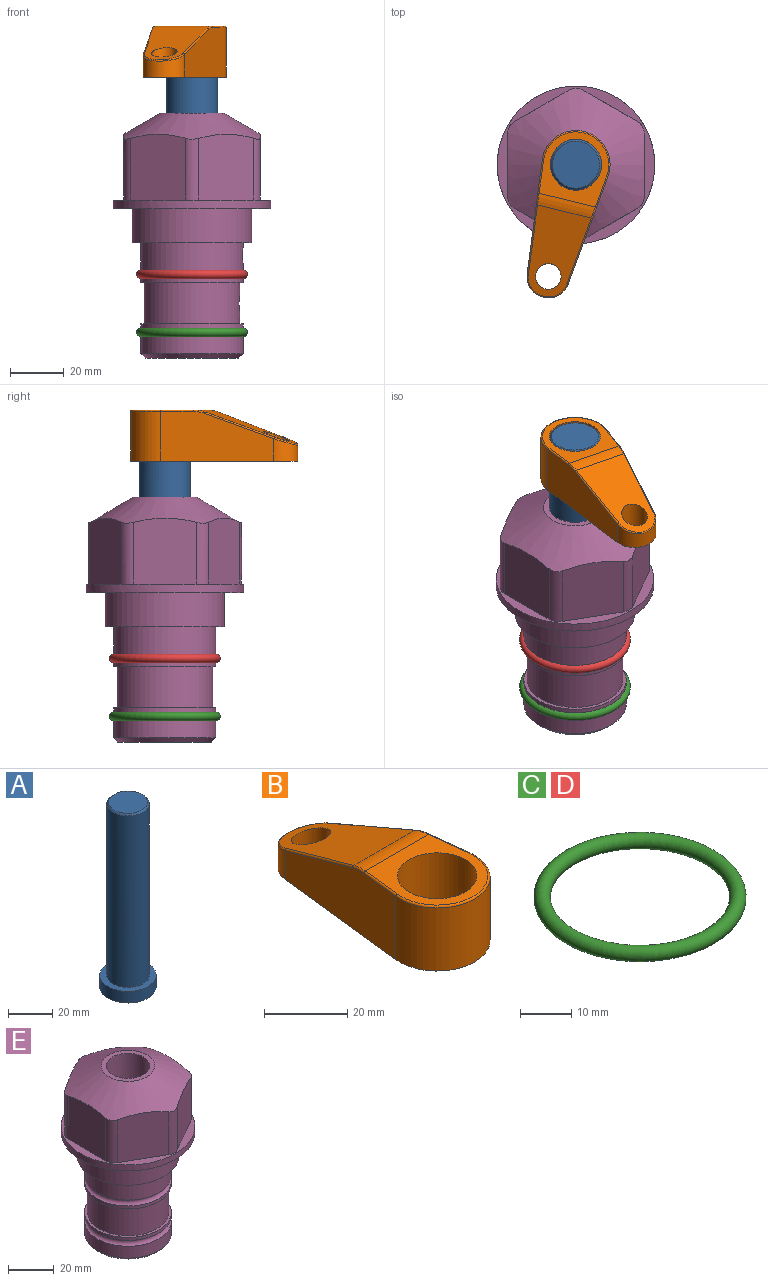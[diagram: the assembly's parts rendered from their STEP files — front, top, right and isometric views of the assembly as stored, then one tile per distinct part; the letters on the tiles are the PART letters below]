
ASSEMBLY  parts=5 mates=3
PART A: 6 faces, bbox 25.4x25.4x101.6 mm
  f0: plane 17.46x17.46mm, normal (0,0,1), area 239.5mm2, adj f5
  f1: plane 25.4x25.4mm, normal (0,0,-1), area 506.7mm2, adj f2
  f2: cylinder r=12.7mm len=25.4mm, axis (0,0,1), area 506.7mm2, adj f1,f3
  f3: plane 25.4x25.4mm, normal (0,0,1), area 221.7mm2, adj f2,f4
  f4: cylinder r=9.53mm len=94.46mm, axis (0,0,1), area 5653mm2, adj f3,f5
  f5: cone r=8.73mm half-angle=45deg, axis (0,0,-1), area 64.4mm2, adj f0,f4
PART B: 44 faces, bbox 27.5x64.5x19.1 mm
  f0: plane 2.3x0.95mm, normal (0,0,-1), area 1mm2, adj f25,f30,f34
  f1: plane 63.5x25.4mm, normal (0,0,-1), area 561.7mm2, adj f2,f3,f4,f5,f6,f7,f19,f20
  f2: cylinder r=12.7mm len=25.4mm, axis (0,0,-1), area 792.2mm2, adj f1,f3,f5,f13
  f3: plane 42.33x18.54mm, normal (0.99,0.11,0), area 647mm2, adj f1,f2,f4,f11,f12,f14
  f4: cylinder r=7.94mm len=15.78mm, axis (0,0,-1), area 158.6mm2, adj f1,f3,f5,f16
  f5: plane 42.33x18.54mm, normal (-0.99,0.11,0), area 647mm2, adj f1,f2,f4,f15,f17,f18
  f6: cylinder r=9.53mm len=19.05mm, axis (0,0,-1), area 1140.1mm2, adj f1,f8
  f7: cylinder r=4.76mm len=10.98mm, axis (0,0,-1), area 276.1mm2, adj f1,f9
  f8: plane 25.83x24.38mm, normal (0,0,1), area 262.2mm2, adj f6,f10,f11,f13,f15
  f9: plane 32.49x20.55mm, normal (0,0.34,0.94), area 489.9mm2, adj f7,f10,f14,f16,f18
  f10: cylinder r=12.7mm len=21.49mm, axis (-1,0,0), area 93.2mm2, adj f8,f9,f12,f17
  f11: cylinder r=0.51mm len=12.34mm, axis (0.11,-0.99,0), area 9.9mm2, adj f3,f8,f12,f13
  f12: bspline ~7.62x1.64mm, area 3.5mm2, adj f3,f10,f11,f14
  f13: torus R=12.19mm, axis (0,0,1), area 33.6mm2, adj f2,f8,f11,f15
  f14: cylinder r=0.51mm len=26.01mm, axis (0.1,-0.93,0.34), area 21.6mm2, adj f3,f9,f12,f16
  f15: cylinder r=0.51mm len=12.34mm, axis (0.11,0.99,0), area 9.9mm2, adj f5,f8,f13,f17
  f16: bspline ~15.78x7.05mm, area 15.7mm2, adj f4,f9,f14,f18
  f17: bspline ~7.62x1.64mm, area 3.5mm2, adj f5,f10,f15,f18
  f18: cylinder r=0.51mm len=26.01mm, axis (0.1,0.93,-0.34), area 21.6mm2, adj f5,f9,f16,f17
  f19: plane 21.6x14.29mm, normal (-0.99,-0.11,0), area 242.6mm2, adj f1,f26,f28,f34,f36,f38
  f20: plane 21.6x14.29mm, normal (0.99,-0.11,0), area 242.6mm2, adj f1,f27,f29,f37,f39,f41
  f21: cylinder r=12.7mm len=14.29mm, axis (0,0,-1), area 173.2mm2, adj f1,f26,f27,f30,f31,f33
  f22: cylinder r=7.94mm len=7.63mm, axis (0,0,-1), area 53.8mm2, adj f1,f28,f29,f42
  f23: plane 2.3x0.95mm, normal (0,0,-1), area 1mm2, adj f25,f33,f37
  f24: plane 17.94x12.32mm, normal (0,-0.34,-0.94), area 191.2mm2, adj f25,f38,f41,f42
  f25: cylinder r=9.53mm len=12.93mm, axis (-1,0,0), area 37.5mm2, adj f0,f23,f24,f31,f36,f39
  f26: cylinder r=1.59mm len=14.29mm, axis (0,0,-1), area 49mm2, adj f1,f19,f21,f32
  f27: cylinder r=1.59mm len=14.29mm, axis (0,0,-1), area 49mm2, adj f1,f20,f21,f35
  f28: cylinder r=1.59mm len=7.28mm, axis (0,0,-1), area 22.1mm2, adj f1,f19,f22,f40
  f29: cylinder r=1.59mm len=7.28mm, axis (0,0,-1), area 22.1mm2, adj f1,f20,f22,f43
  f30: torus R=14.29mm, axis (0,0,1), area 5.8mm2, adj f0,f21,f31,f32
  f31: bspline ~11.06x2.73mm, area 20.8mm2, adj f21,f25,f30,f33
  f32: sphere r=1.59mm, area 5.4mm2, adj f26,f30,f34
  f33: torus R=14.29mm, axis (0,0,1), area 5.8mm2, adj f21,f23,f31,f35
  f34: cylinder r=1.59mm len=1.68mm, axis (-0.11,0.99,0), area 2.4mm2, adj f0,f19,f32,f36
  f35: sphere r=1.59mm, area 5.4mm2, adj f27,f33,f37
  f36: bspline ~5.82x2.33mm, area 7.7mm2, adj f19,f25,f34,f38
  f37: cylinder r=1.59mm len=1.68mm, axis (0.11,0.99,0), area 2.4mm2, adj f20,f23,f35,f39
  f38: cylinder r=1.59mm len=18.33mm, axis (0.1,-0.93,0.34), area 46.7mm2, adj f19,f24,f36,f40
  f39: bspline ~5.82x2.33mm, area 7.7mm2, adj f20,f25,f37,f41
  f40: sphere r=1.59mm, area 3.6mm2, adj f28,f38,f42
  f41: cylinder r=1.59mm len=18.33mm, axis (0.1,0.93,-0.34), area 46.7mm2, adj f20,f24,f39,f43
  f42: bspline ~8.31x1.84mm, area 15.3mm2, adj f22,f24,f40,f43
  f43: sphere r=1.59mm, area 3.6mm2, adj f29,f41,f42
PART C: 1 faces, bbox 44.7x44.7x3.2 mm
  f0: torus R=19.05mm, axis (0,0,1), area 1193.9mm2
PART D: same geometry as C
PART E: 36 faces, bbox 58.7x58.7x91.2 mm
  f0: cylinder r=17.78mm len=35.56mm, axis (0,0,1), area 1670.8mm2, adj f23,f24,f31
  f1: cylinder r=19.05mm len=38.1mm, axis (0,0,1), area 1191.9mm2, adj f26,f27,f30
  f2: plane 58.66x58.66mm, normal (0,0,-1), area 1150.6mm2, adj f3,f28
  f3: cylinder r=29.33mm len=58.66mm, axis (0,0,-1), area 585.1mm2, adj f2,f4
  f4: plane 58.66x58.66mm, normal (0,0,1), area 475.9mm2, adj f3,f5,f6,f7,f8,f9,f10,f11
  f5: plane 24.5x20.32mm, normal (-0.5,0.87,0), area 562.8mm2, adj f4,f15,f16,f17
  f6: plane 24.5x20.32mm, normal (0.5,0.87,0), area 562.8mm2, adj f4,f14,f15,f17
  f7: plane 24.5x23.48mm, normal (1,0,0), area 562.8mm2, adj f4,f13,f14,f17
  f8: plane 24.5x20.32mm, normal (0.5,-0.87,0), area 562.8mm2, adj f4,f12,f13,f17
  f9: plane 24.5x20.32mm, normal (-0.5,-0.87,0), area 562.8mm2, adj f4,f11,f12,f17
  f10: plane 24.5x23.48mm, normal (-1,0,0), area 562.8mm2, adj f4,f11,f16,f17
  f11: cylinder r=5.08mm len=23.01mm, axis (0,0,-1), area 121.2mm2, adj f4,f9,f10,f17
  f12: cylinder r=5.08mm len=23.01mm, axis (0,0,-1), area 121.2mm2, adj f4,f8,f9,f17
  f13: cylinder r=5.08mm len=23.01mm, axis (0,0,-1), area 121.2mm2, adj f4,f7,f8,f17
  f14: cylinder r=5.08mm len=23.01mm, axis (0,0,-1), area 121.2mm2, adj f4,f6,f7,f17
  f15: cylinder r=5.08mm len=23.01mm, axis (0,0,-1), area 121.2mm2, adj f4,f5,f6,f17
  f16: cylinder r=5.08mm len=23.01mm, axis (0,0,-1), area 121.2mm2, adj f4,f5,f10,f17
  f17: cone r=11.73mm half-angle=60deg, axis (0,0,-1), area 2071.8mm2, adj f5,f6,f7,f8,f9,f10,f11,f12
  f18: plane 23.46x23.46mm, normal (0,0,1), area 147.4mm2, adj f17,f35
  f19: plane 34.93x34.93mm, normal (0,0,-1), area 958mm2, adj f29
  f20: cylinder r=19.05mm len=38.1mm, axis (0,0,1), area 760.1mm2, adj f21,f29
  f21: torus R=19.05mm, axis (0,0,1), area 565.3mm2, adj f20,f22
  f22: cylinder r=19.05mm len=38.1mm, axis (0,0,1), area 190mm2, adj f21,f23
  f23: plane 38.1x38.1mm, normal (0,0,1), area 146.9mm2, adj f0,f22
  f24: plane 38.1x38.1mm, normal (0,0,-1), area 146.9mm2, adj f0,f25
  f25: cylinder r=19.05mm len=38.1mm, axis (0,0,1), area 190mm2, adj f24,f26
  f26: torus R=19.05mm, axis (0,0,1), area 565.3mm2, adj f1,f25
  f27: plane 44.45x44.45mm, normal (0,0,-1), area 411.7mm2, adj f1,f28
  f28: cylinder r=22.23mm len=44.45mm, axis (0,0,1), area 1773.5mm2, adj f2,f27
  f29: cone r=19.05mm half-angle=45deg, axis (0,0,1), area 257.5mm2, adj f19,f20
  f30: cylinder r=3.17mm len=6.75mm, axis (-1,0,0), area 128mm2, adj f1,f33
  f31: cylinder r=3.17mm len=6.35mm, axis (-1,0,0), area 102.5mm2, adj f0,f33
  f32: plane 25.4x25.4mm, normal (0,0,1), area 506.7mm2, adj f33
  f33: cylinder r=12.7mm len=66.42mm, axis (0,0,-1), area 5236.2mm2, adj f30,f31,f32,f34
  f34: cone r=9.53mm half-angle=30deg, axis (0,0,-1), area 443.4mm2, adj f33,f35
  f35: cylinder r=9.53mm len=19.05mm, axis (0,0,-1), area 849mm2, adj f18,f34
PLACE A rot(axis=(0,0,-1),103.9deg) t=(0,0,-5.69)mm
PLACE B rot(axis=(0,0,1),166.1deg) t=(0,0,48.92)mm
PLACE C t=(0,0,-21.59)mm
PLACE D at identity
PLACE E at identity fixed
MATE fastened C.f0 <-> E.f0  axis (0,0,1) through (0,0,-46.1)mm
MATE cylindrical A.f2 <-> E.f0  axis (0,0,1) through (0,0,19.95)mm
MATE fastened B.f2 <-> A.f2  axis (0,0,1) through (0,0,67.97)mm
